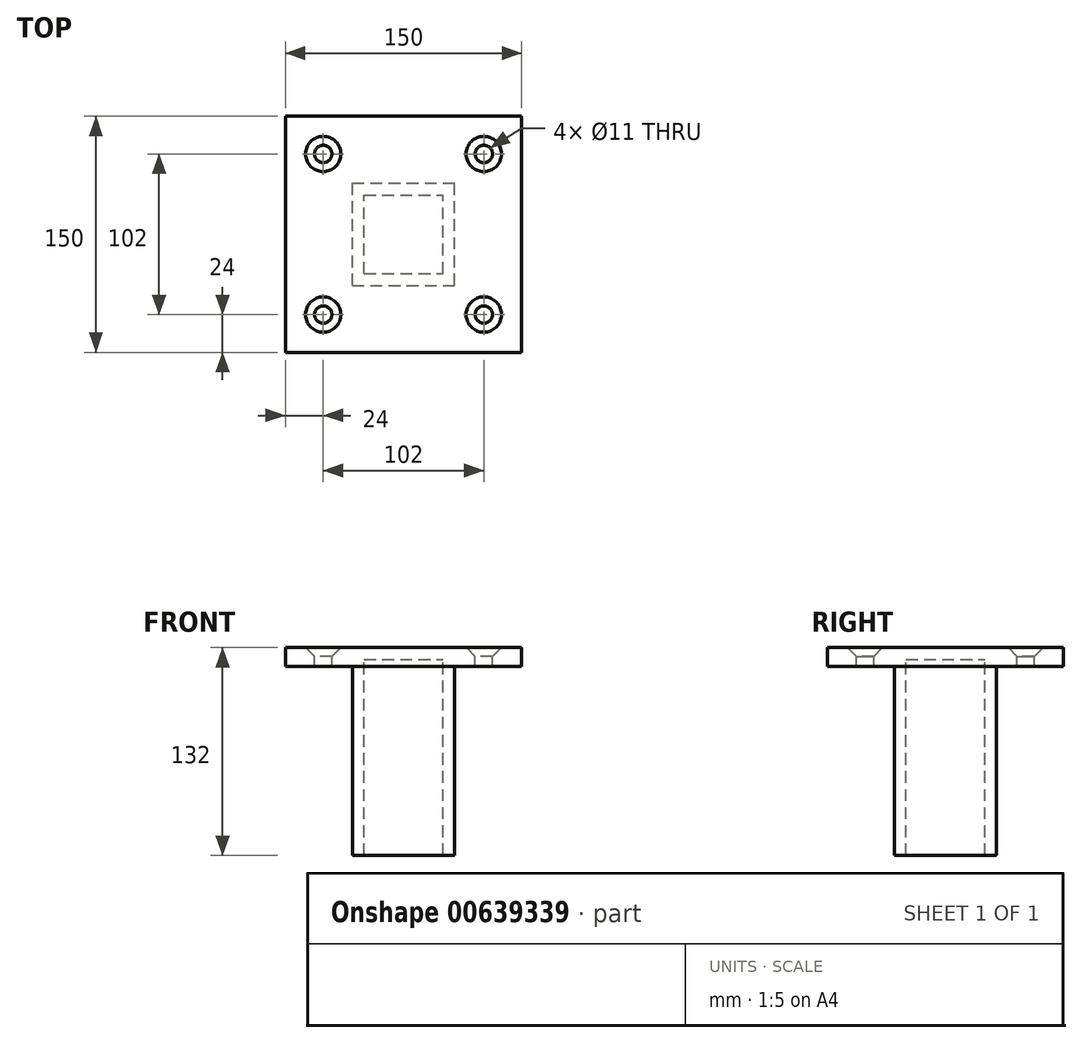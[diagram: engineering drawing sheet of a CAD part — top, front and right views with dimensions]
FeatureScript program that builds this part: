
annotation { "Feature Type Name" : "Feature", "Feature Type Description" : "" }
export const myFeature = defineFeature(function(context is Context, id is Id, definition is map)
    precondition{}
    {
        {
            var Q0;
            Q0=qCreatedBy(makeId("Top.planeOp"),FACE);
            var sketch = newSketch(context, id + "F0", { "sketchPlane" : qUnion([Q0])});
            skLineSegment(sketch, "E0.bottom", {"start": v(-75, 75) * mm, "end": v(75, 75) * mm});
            skLineSegment(sketch, "E0.top", {"start": v(-75, -75) * mm, "end": v(75, -75) * mm});
            skLineSegment(sketch, "E0.left", {"start": v(-75, 75) * mm, "end": v(-75, -75) * mm});
            skLineSegment(sketch, "E0.right", {"start": v(75, 75) * mm, "end": v(75, -75) * mm});
            skSolve(sketch);
        }
        {
            var Q0;
            Q0=makeQuery(id+"F0.imprint","IMPRINT",FACE,{"disambiguationData":[TD([[makeQuery(id+"F0.imprint","IMPRINT",EDGE,{"derivedFrom":sQuery(id+"F0.wireOp",EDGE,"E0.bottom")}),-1.0]])]});
            extrude(context, id + "F1", {"entities" : qUnion([Q0]), "depth" : 6 * mm, "offsetDistance" : 25 * mm, "hasSecondDirection" : true, "secondDirectionOppositeDirection" : true, "secondDirectionDepth" : 6 * mm});
        }
        {
            var Q0;
            Q0=makeQuery(id+"F1.opExtrude","CAP_FACE",FACE,{"disambiguationData":[OSD([sQuery(id+"F0.wireOp",EDGE,"E0.bottom"),sQuery(id+"F0.wireOp",EDGE,"E0.top"),sQuery(id+"F0.wireOp",EDGE,"E0.left"),sQuery(id+"F0.wireOp",EDGE,"E0.right")])],"isStart":false});
            var sketch = newSketch(context, id + "F2", { "sketchPlane" : qUnion([Q0])});
            skCircle(sketch, "E1", {"center": v(-51, 51) * mm, "radius": 11.54 * mm});
            skCircle(sketch, "E2", {"center": v(51, 51) * mm, "radius": 10.35 * mm});
            skCircle(sketch, "E3", {"center": v(51, -51) * mm, "radius": 11.01 * mm});
            skCircle(sketch, "E4", {"center": v(-51, -51) * mm, "radius": 12.17 * mm});
            skLineSegment(sketch, "E5.bottom", {"start": v(-25, 25) * mm, "end": v(25, 25) * mm});
            skLineSegment(sketch, "E5.top", {"start": v(-25, -25) * mm, "end": v(25, -25) * mm});
            skLineSegment(sketch, "E5.left", {"start": v(-25, 25) * mm, "end": v(-25, -25) * mm});
            skLineSegment(sketch, "E5.right", {"start": v(25, 25) * mm, "end": v(25, -25) * mm});
            skSolve(sketch);
        }
        {
            var Q0;
            Q0=sQuery(id+"F2.wireOp",VERTEX,"E1.center");
            var Q1;
            Q1=sQuery(id+"F2.wireOp",VERTEX,"E2.center");
            var Q2;
            Q2=sQuery(id+"F2.wireOp",VERTEX,"E3.center");
            var Q3;
            Q3=sQuery(id+"F2.wireOp",VERTEX,"E4.center");
            var Q4;
            Q4=makeQuery(id+"F1.opExtrude","SWEPT_BODY",BODY,{"disambiguationData":[OSD([sQuery(id+"F0.wireOp",EDGE,"E0.bottom"),sQuery(id+"F0.wireOp",EDGE,"E0.top"),sQuery(id+"F0.wireOp",EDGE,"E0.left"),sQuery(id+"F0.wireOp",EDGE,"E0.right")])]});
            hole(context, id + "F3", {"style" : HoleStyle.C_SINK, "endStyle" : HoleEndStyle.THROUGH, "standardTappedOrClearance" : lookupTablePath({ "standard" : "ISO", "fit" : "Normal", "size" : "M10", "type" : "Clearance" }), "standardBlindInLast" : lookupTablePath({ "fit" : "Standard", "standard" : "ISO", "size" : "M10", "type" : "Clearance" }), "holeDiameter" : 11 * mm, "cSinkDiameter" : 22.4 * mm, "cSinkAngle" : 90 * degree, "majorDiameter" : 5 * mm, "isTappedThrough" : true, "tappedDepth" : 12 * mm, "tapClearance" : 3, "startFromSketch" : true, "locations" : qUnion([Q0, Q1, Q2, Q3]), "scope" : qUnion([Q4])});
        }
        {
            var Q0;
            Q0=makeQuery(id+"F1.opExtrude","CAP_FACE",FACE,{"disambiguationData":[OSD([sQuery(id+"F0.wireOp",EDGE,"E0.bottom"),sQuery(id+"F0.wireOp",EDGE,"E0.top"),sQuery(id+"F0.wireOp",EDGE,"E0.left"),sQuery(id+"F0.wireOp",EDGE,"E0.right")])],"isStart":true});
            var sketch = newSketch(context, id + "F4", { "sketchPlane" : qUnion([Q0])});
            skLineSegment(sketch, "E6.bottom", {"start": v(-32.5, 32.5) * mm, "end": v(32.5, 32.5) * mm});
            skLineSegment(sketch, "E6.top", {"start": v(-32.5, -32.5) * mm, "end": v(32.5, -32.5) * mm});
            skLineSegment(sketch, "E6.left", {"start": v(-32.5, 32.5) * mm, "end": v(-32.5, -32.5) * mm});
            skLineSegment(sketch, "E6.right", {"start": v(32.5, 32.5) * mm, "end": v(32.5, -32.5) * mm});
            skSolve(sketch);
        }
        {
            var Q0;
            Q0 = qSketchRegion(id + "F4", true);
            extrude(context, id + "F5", {"entities" : qUnion([Q0]), "operationType" : NewBodyOperationType.ADD, "depth" : 120 * mm, "offsetDistance" : 25 * mm});
        }
        {
            var Q0;
            Q0=makeQuery(id+"F5.opExtrude","CAP_FACE",FACE,{"disambiguationData":[OSD([sQuery(id+"F4.wireOp",EDGE,"E6.bottom"),sQuery(id+"F4.wireOp",EDGE,"E6.top"),sQuery(id+"F4.wireOp",EDGE,"E6.left"),sQuery(id+"F4.wireOp",EDGE,"E6.right")])],"isStart":false});
            shell(context, id + "F6", {"entities" : qUnion([Q0]), "thickness" : 7.5 * mm});
        }
    });
